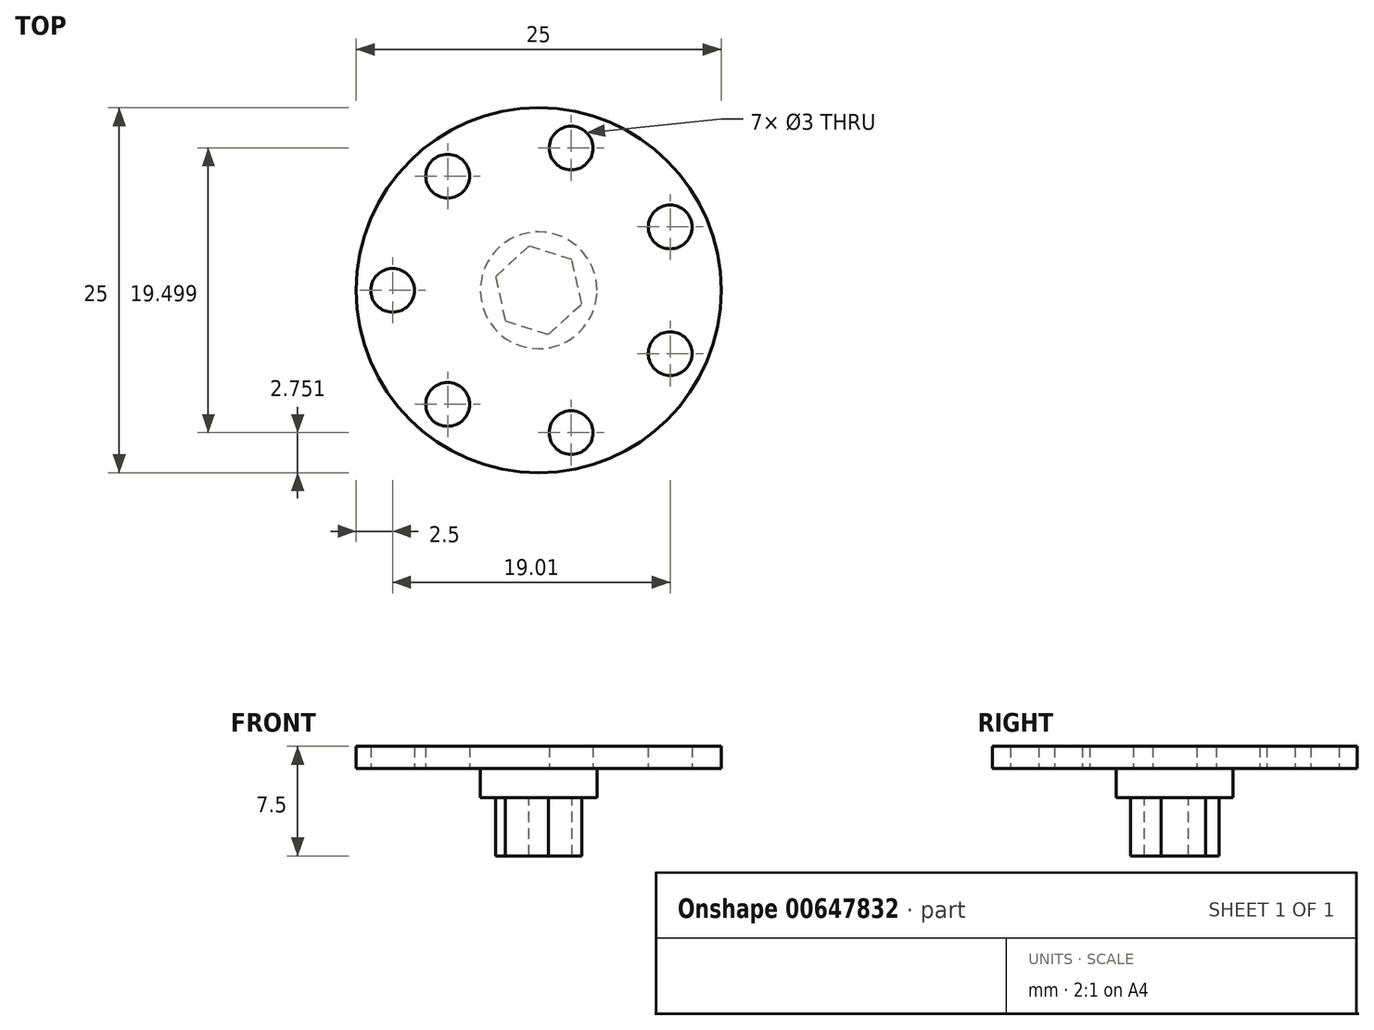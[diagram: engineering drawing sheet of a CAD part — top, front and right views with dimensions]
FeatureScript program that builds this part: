
annotation { "Feature Type Name" : "Feature", "Feature Type Description" : "" }
export const myFeature = defineFeature(function(context is Context, id is Id, definition is map)
    precondition{}
    {
        {
            var Q0;
            Q0=qCreatedBy(makeId("Top.planeOp"),FACE);
            var sketch = newSketch(context, id + "F0", { "sketchPlane" : qUnion([Q0])});
            skCircle(sketch, "E0", {"center": v(0, 0) * mm, "radius": 12.5 * mm});
            skCircle(sketch, "E1", {"center": v(0, 0) * mm, "radius": 4 * mm});
            skCircle(sketch, "E2", {"center": v(0, 0) * mm, "radius": 10 * mm, "construction": true});
            skCircle(sketch, "E3", {"center": v(-10, 0) * mm, "radius": 1.5 * mm});
            skCircle(sketch, "E4.1.0", {"center": v(-6.23, -7.82) * mm, "radius": 1.5 * mm});
            skCircle(sketch, "E4.2.0", {"center": v(2.23, -9.75) * mm, "radius": 1.5 * mm});
            skCircle(sketch, "E4.3.0", {"center": v(9, -4.34) * mm, "radius": 1.5 * mm});
            skCircle(sketch, "E4.4.0", {"center": v(9, 4.34) * mm, "radius": 1.5 * mm});
            skCircle(sketch, "E4.5.0", {"center": v(2.23, 9.75) * mm, "radius": 1.5 * mm});
            skCircle(sketch, "E4.6.0", {"center": v(-6.23, 7.82) * mm, "radius": 1.5 * mm});
            skSolve(sketch);
        }
        {
            var Q0;
            Q0 = qSketchRegion(id + "F0", true);
            var Q1;
            Q1=makeQuery(id+"F0.imprint","IMPRINT",FACE,{"disambiguationData":[TD([[makeQuery(id+"F0.imprint","IMPRINT",EDGE,{"derivedFrom":sQuery(id+"F0.wireOp",EDGE,"E1")}),1.0]])]});
            extrude(context, id + "F1", {"entities" : qUnion([Q0, Q1]), "depth" : 1.5 * mm, "offsetDistance" : 25 * mm});
        }
        {
            var Q0;
            Q0=makeQuery(id+"F0.imprint","IMPRINT",FACE,{"disambiguationData":[TD([[makeQuery(id+"F0.imprint","IMPRINT",EDGE,{"derivedFrom":sQuery(id+"F0.wireOp",EDGE,"E1")}),1.0]])]});
            extrude(context, id + "F2", {"entities" : qUnion([Q0]), "operationType" : NewBodyOperationType.ADD, "oppositeDirection" : true, "depth" : 2 * mm, "offsetDistance" : 25 * mm});
        }
        {
            var Q0;
            Q0=makeQuery(id+"F2.opExtrude","CAP_FACE",FACE,{"disambiguationData":[OSD([sQuery(id+"F0.wireOp",EDGE,"E1")])],"isStart":false});
            var sketch = newSketch(context, id + "F3", { "sketchPlane" : qUnion([Q0])});
            skPoint(sketch, "E5.middle", {"position": v(0, 0) * mm});
            skCircle(sketch, "E6.cCircle", {"center": v(0, 0) * mm, "radius": 3.1 * mm, "construction": true});
            skLineSegment(sketch, "E6.0", {"start": v(2.28, -2.1) * mm, "end": v(-0.67, -3.03) * mm});
            skLineSegment(sketch, "E6.1", {"start": v(-0.67, -3.03) * mm, "end": v(-2.96, -0.93) * mm});
            skLineSegment(sketch, "E6.2", {"start": v(-2.96, -0.93) * mm, "end": v(-2.28, 2.1) * mm});
            skLineSegment(sketch, "E6.3", {"start": v(-2.28, 2.1) * mm, "end": v(0.67, 3.03) * mm});
            skLineSegment(sketch, "E6.4", {"start": v(0.67, 3.03) * mm, "end": v(2.96, 0.93) * mm});
            skLineSegment(sketch, "E6.5", {"start": v(2.96, 0.93) * mm, "end": v(2.28, -2.1) * mm});
            skSolve(sketch);
        }
        {
            var Q0;
            Q0 = qSketchRegion(id + "F3", true);
            extrude(context, id + "F4", {"entities" : qUnion([Q0]), "operationType" : NewBodyOperationType.ADD, "depth" : 4 * mm, "offsetDistance" : 25 * mm});
        }
    });
